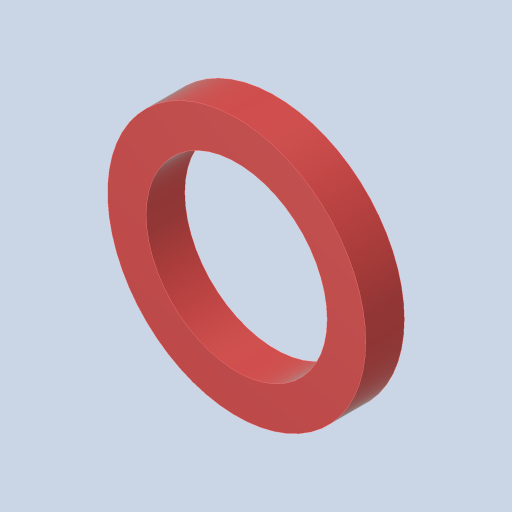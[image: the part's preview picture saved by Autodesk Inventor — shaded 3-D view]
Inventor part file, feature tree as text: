
AUTODESK INVENTOR PART (.ipt)
format: ipt  version: 2023.4 (Build 274418000, 418)  size: 121,856 bytes
history: native  units: in
note: dims shown in document units (in); Inventor stores cm internally (conversion verified against a paired STEP export)
features: extrude x1, sketch x1
ambient origin geometry x8: Origin, YZ Plane, XZ Plane, XY Plane, X Axis, Y Axis, Z Axis, Center Point
bodies: Solid1 (feature_tree)
feature tree (2):
  extrude  "Extrusion1"  Depth=0.125in
  sketch  "Sketch1"  dims[d0=0.585in d1=0.125in d2=0.125in d3=0.0in]
